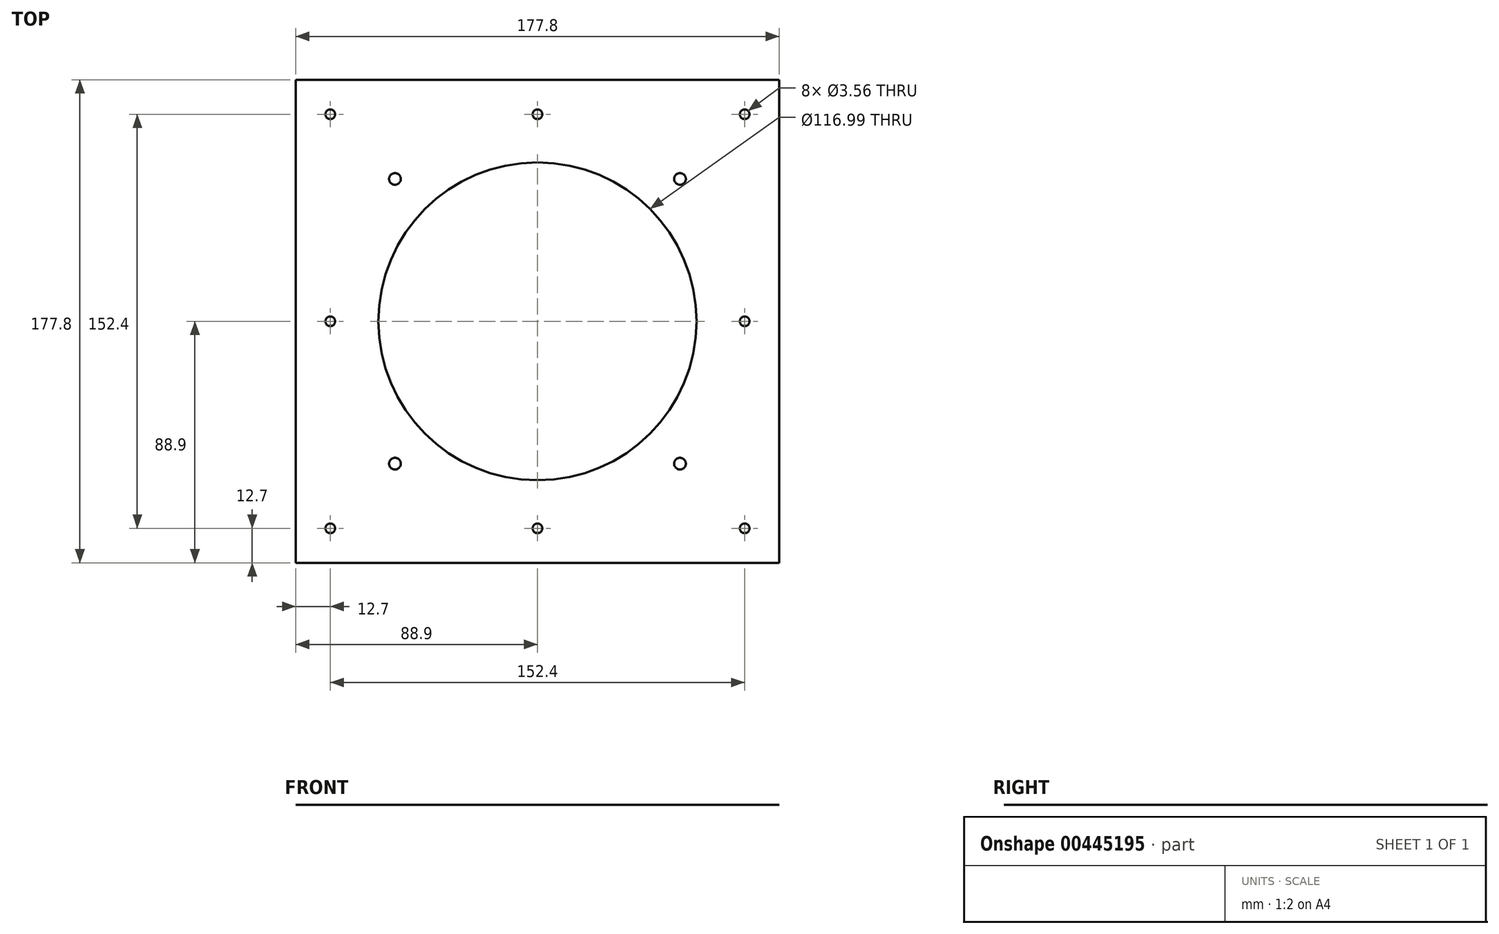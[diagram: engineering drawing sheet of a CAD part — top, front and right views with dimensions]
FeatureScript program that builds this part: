
annotation { "Feature Type Name" : "Feature", "Feature Type Description" : "" }
export const myFeature = defineFeature(function(context is Context, id is Id, definition is map)
    precondition{}
    {
        {
            var Q0;
            Q0=qCreatedBy(makeId("Top.planeOp"),FACE);
            var sketch = newSketch(context, id + "F0", { "sketchPlane" : qUnion([Q0])});
            skLineSegment(sketch, "E0.bottom", {"start": v(0, 0) * mm, "end": v(177.8, 0) * mm});
            skLineSegment(sketch, "E0.top", {"start": v(0, 177.8) * mm, "end": v(177.8, 177.8) * mm});
            skLineSegment(sketch, "E0.left", {"start": v(0, 0) * mm, "end": v(0, 177.8) * mm});
            skLineSegment(sketch, "E0.right", {"start": v(177.8, 0) * mm, "end": v(177.8, 177.8) * mm});
            skLineSegment(sketch, "E1.bottom", {"start": v(141.3, 141.3) * mm, "end": v(36.5, 141.3) * mm, "construction": true});
            skLineSegment(sketch, "E1.top", {"start": v(141.3, 36.5) * mm, "end": v(36.5, 36.5) * mm, "construction": true});
            skLineSegment(sketch, "E1.left", {"start": v(141.3, 141.3) * mm, "end": v(141.3, 36.5) * mm, "construction": true});
            skLineSegment(sketch, "E1.right", {"start": v(36.5, 141.3) * mm, "end": v(36.5, 36.5) * mm, "construction": true});
            skLineSegment(sketch, "E2", {"start": v(177.8, 177.8) * mm, "end": v(0, 0) * mm, "construction": true});
            skLineSegment(sketch, "E3", {"start": v(141.3, 36.5) * mm, "end": v(36.5, 141.3) * mm, "construction": true});
            skPoint(sketch, "E4", {"position": v(88.9, 88.9) * mm});
            skCircle(sketch, "E5", {"center": v(88.9, 88.9) * mm, "radius": 58.5 * mm});
            skCircle(sketch, "E6", {"center": v(141.3, 141.3) * mm, "radius": 2.16 * mm});
            skCircle(sketch, "E7.1.0", {"center": v(36.5, 141.3) * mm, "radius": 2.16 * mm});
            skCircle(sketch, "E7.2.0", {"center": v(36.5, 36.5) * mm, "radius": 2.16 * mm});
            skCircle(sketch, "E7.3.0", {"center": v(141.3, 36.5) * mm, "radius": 2.16 * mm});
            skLineSegment(sketch, "E8.bottom", {"start": v(25.4, 152.4) * mm, "end": v(152.4, 152.4) * mm, "construction": true});
            skLineSegment(sketch, "E8.top", {"start": v(25.4, 25.4) * mm, "end": v(152.4, 25.4) * mm, "construction": true});
            skLineSegment(sketch, "E8.left", {"start": v(25.4, 152.4) * mm, "end": v(25.4, 25.4) * mm, "construction": true});
            skLineSegment(sketch, "E8.right", {"start": v(152.4, 152.4) * mm, "end": v(152.4, 25.4) * mm, "construction": true});
            skCircle(sketch, "E9", {"center": v(165.1, 165.1) * mm, "radius": 1.78 * mm});
            skCircle(sketch, "E10.0.1.0", {"center": v(165.1, 88.9) * mm, "radius": 1.78 * mm});
            skCircle(sketch, "E10.0.2.0", {"center": v(165.1, 12.7) * mm, "radius": 1.78 * mm});
            skCircle(sketch, "E10.1.0.0", {"center": v(88.9, 165.1) * mm, "radius": 1.78 * mm});
            skCircle(sketch, "E10.1.1.0", {"center": v(88.9, 88.9) * mm, "radius": 1.78 * mm});
            skCircle(sketch, "E10.1.2.0", {"center": v(88.9, 12.7) * mm, "radius": 1.78 * mm});
            skCircle(sketch, "E10.2.0.0", {"center": v(12.7, 165.1) * mm, "radius": 1.78 * mm});
            skCircle(sketch, "E10.2.1.0", {"center": v(12.7, 88.9) * mm, "radius": 1.78 * mm});
            skCircle(sketch, "E10.2.2.0", {"center": v(12.7, 12.7) * mm, "radius": 1.78 * mm});
            skLineSegment(sketch, "E10.direction1", {"start": v(165.1, 165.1) * mm, "end": v(88.9, 165.1) * mm, "construction": true});
            skLineSegment(sketch, "E10.direction2", {"start": v(165.1, 165.1) * mm, "end": v(165.1, 88.9) * mm, "construction": true});
            skSolve(sketch);
        }
        {
            var Q0;
            Q0=makeQuery(id+"F0.imprint","IMPRINT",FACE,{"disambiguationData":[TD([[makeQuery(id+"F0.imprint","IMPRINT",EDGE,{"derivedFrom":sQuery(id+"F0.wireOp",EDGE,"E0.bottom")}),1.0]])]});
            extrude(context, id + "F1", {"entities" : qUnion([Q0]), "depth" : 1 / 203.2 * mm});
        }
    });
